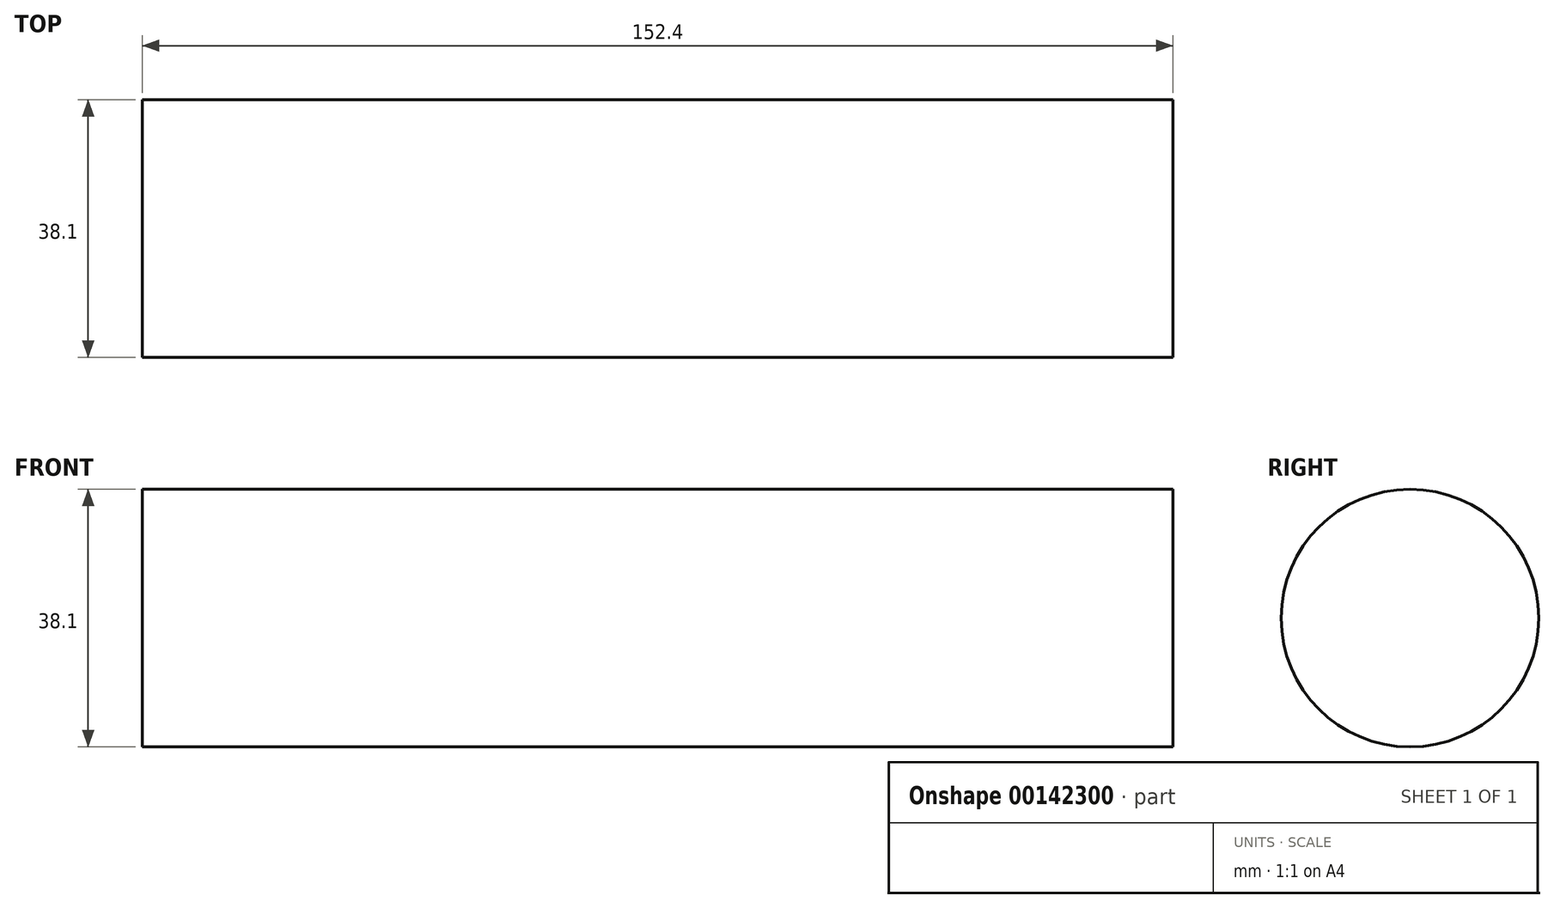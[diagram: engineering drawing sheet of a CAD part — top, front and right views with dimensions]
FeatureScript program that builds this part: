
annotation { "Feature Type Name" : "Feature", "Feature Type Description" : "" }
export const myFeature = defineFeature(function(context is Context, id is Id, definition is map)
    precondition{}
    {
        {
            var Q0;
            Q0=qCreatedBy(makeId("Right.planeOp"),FACE);
            var sketch = newSketch(context, id + "F0", { "sketchPlane" : qUnion([Q0])});
            skCircle(sketch, "E0", {"center": v(0, 0) * mm, "radius": 19.05 * mm});
            skSolve(sketch);
        }
        {
            var Q0;
            Q0 = qSketchRegion(id + "F0", true);
            extrude(context, id + "F1", {"entities" : qUnion([Q0]), "depth" : 76.2 * mm, "hasSecondDirection" : true, "secondDirectionOppositeDirection" : true, "secondDirectionDepth" : 76.2 * mm});
        }
    });
